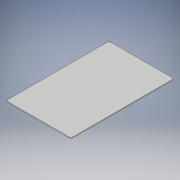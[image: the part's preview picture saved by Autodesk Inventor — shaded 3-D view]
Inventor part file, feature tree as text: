
AUTODESK INVENTOR PART (.ipt)
format: ipt  version: 2019.4 (Build 234330000, 330)  size: 103,424 bytes
history: native  units: in
note: dims shown in document units (in); Inventor stores cm internally (conversion verified against a paired STEP export)
features: fillet x3, extrude x1, sketch x1
ambient origin geometry x8: Origin, YZ Plane, XZ Plane, XY Plane, X Axis, Y Axis, Z Axis, Center Point
bodies: Solid1 (feature_tree)
feature tree (5):
  extrude  "Extrusion1"  Depth=2.125in
  fillet  "Fillet1"  Radius=1.685in
  fillet  "Fillet2"  Radius=1.0625in
  fillet  "Fillet3"  Radius=0.024in
  sketch  "Sketch1"  dims[d0=3.37in d1=2.125in d2=1.685in d3=1.0625in d4=0.024in d5=0.0in d6=0.05in d7=0.05in d8=0.05in]
